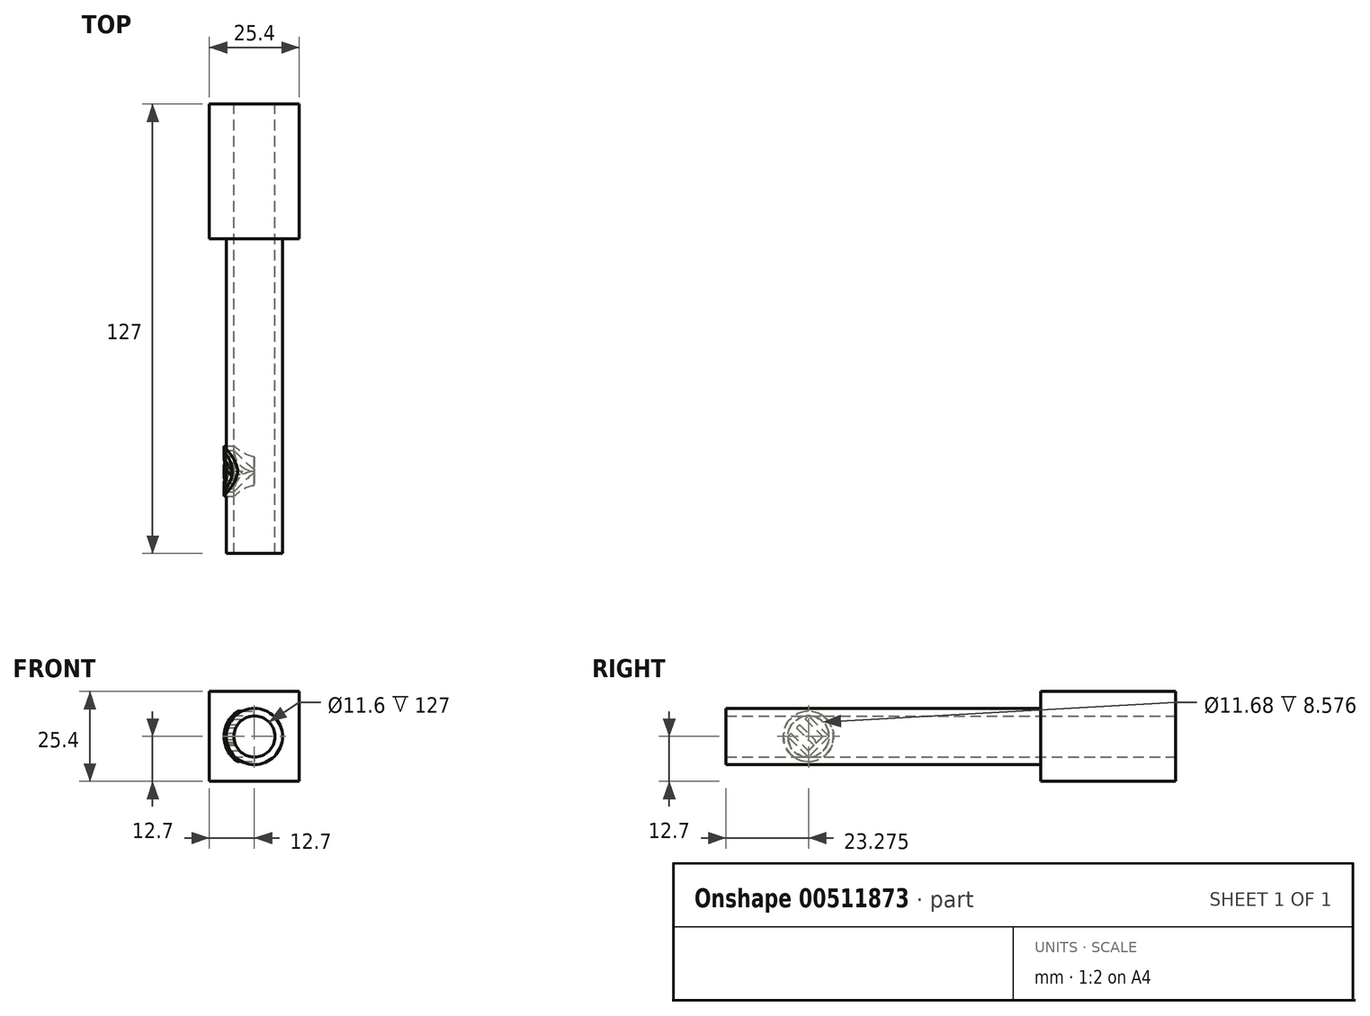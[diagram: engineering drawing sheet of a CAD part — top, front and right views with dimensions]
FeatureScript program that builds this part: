
annotation { "Feature Type Name" : "Feature", "Feature Type Description" : "" }
export const myFeature = defineFeature(function(context is Context, id is Id, definition is map)
    precondition{}
    {
        {
            var Q0;
            Q0=qCreatedBy(makeId("Front.planeOp"),FACE);
            var sketch = newSketch(context, id + "F0", { "sketchPlane" : qUnion([Q0])});
            skLineSegment(sketch, "E0.bottom", {"start": v(12.7, -12.7) * mm, "end": v(-12.7, -12.7) * mm});
            skLineSegment(sketch, "E0.top", {"start": v(12.7, 12.7) * mm, "end": v(-12.7, 12.7) * mm});
            skLineSegment(sketch, "E0.left", {"start": v(12.7, -12.7) * mm, "end": v(12.7, 12.7) * mm});
            skLineSegment(sketch, "E0.right", {"start": v(-12.7, -12.7) * mm, "end": v(-12.7, 12.7) * mm});
            skPoint(sketch, "E0.middle", {"position": v(0, 0) * mm});
            skCircle(sketch, "E1", {"center": v(0, 0) * mm, "radius": 7.94 * mm});
            skCircle(sketch, "E2", {"center": v(0, 0) * mm, "radius": 5.8 * mm});
            skSolve(sketch);
        }
        {
            var Q0;
            Q0=qSketchRegion(id+"F0",true);
            var Q1;
            Q1=makeQuery(id+"F0.imprint","IMPRINT",FACE,{"disambiguationData":[TD([[makeQuery(id+"F0.imprint","IMPRINT",EDGE,{"derivedFrom":sQuery(id+"F0.wireOp",EDGE,"E1")}),1.0]])]});
            extrude(context, id + "F1", {"entities" : qUnion([Q0, Q1]), "depth" : 38.1 * mm});
        }
        {
            var Q0;
            Q0=makeQuery(id+"F0.imprint","IMPRINT",FACE,{"disambiguationData":[TD([[makeQuery(id+"F0.imprint","IMPRINT",EDGE,{"derivedFrom":sQuery(id+"F0.wireOp",EDGE,"E1")}),1.0]])]});
            extrude(context, id + "F2", {"entities" : qUnion([Q0]), "operationType" : NewBodyOperationType.ADD, "depth" : 127 * mm, "offsetDistance" : 25.4 * mm});
        }
        {
            var Q0;
            Q0=qCreatedBy(makeId("Right.planeOp"),FACE);
            var sketch = newSketch(context, id + "F3", { "sketchPlane" : qUnion([Q0])});
            skCircle(sketch, "E3", {"center": v(-103.72, 0) * mm, "radius": 7.11 * mm});
            skCircle(sketch, "E4", {"center": v(-103.72, 0) * mm, "radius": 5.84 * mm});
            skLineSegment(sketch, "E5", {"start": v(-97.88, 0) * mm, "end": v(-103.72, 5.84) * mm});
            skLineSegment(sketch, "E6", {"start": v(-103.72, 5.84) * mm, "end": v(-104.62, 4.94) * mm});
            skLineSegment(sketch, "E7", {"start": v(-97.88, 0) * mm, "end": v(-103.72, -5.84) * mm});
            skLineSegment(sketch, "E8", {"start": v(-103.72, -5.84) * mm, "end": v(-109.57, 0) * mm});
            skLineSegment(sketch, "E9", {"start": v(-109.57, 0) * mm, "end": v(-108.67, 0.9) * mm});
            skLineSegment(sketch, "E10", {"start": v(-104.62, 4.94) * mm, "end": v(-99.68, 0) * mm});
            skLineSegment(sketch, "E11", {"start": v(-99.68, 0) * mm, "end": v(-101.28, -1.6) * mm});
            skLineSegment(sketch, "E12", {"start": v(-106.21, 3.34) * mm, "end": v(-107.1, 2.44) * mm});
            skLineSegment(sketch, "E13", {"start": v(-107.1, 2.44) * mm, "end": v(-102.17, -2.5) * mm});
            skLineSegment(sketch, "E14", {"start": v(-108.67, 0.9) * mm, "end": v(-103.73, -4.04) * mm});
            skLineSegment(sketch, "E15", {"start": v(-103.73, -4.04) * mm, "end": v(-102.17, -2.5) * mm});
            skLineSegment(sketch, "E16", {"start": v(-102, -0.87) * mm, "end": v(-101.63, -1.96) * mm});
            skLineSegment(sketch, "E17", {"start": v(-101.63, -1.96) * mm, "end": v(-101.28, -1.6) * mm});
            skLineSegment(sketch, "E18", {"start": v(-106.21, 3.34) * mm, "end": v(-102, -0.87) * mm});
            skSolve(sketch);
        }
        {
            var Q0;
            Q0=makeQuery(id+"F3.imprint","IMPRINT",FACE,{"disambiguationData":[TD([[makeQuery(id+"F3.imprint","IMPRINT",EDGE,{"derivedFrom":sQuery(id+"F3.wireOp",EDGE,"E3")}),1.0]])]});
            var Q1;
            Q1=makeQuery(id+"F3.imprint","IMPRINT",FACE,{"disambiguationData":[TD([[makeQuery(id+"F3.imprint","IMPRINT",EDGE,{"derivedFrom":sQuery(id+"F3.wireOp",EDGE,"E5")}),1.0]])]});
            extrude(context, id + "F4", {"entities" : qUnion([Q0, Q1]), "oppositeDirection" : true, "depth" : 12.7 * mm, "offsetDistance" : 25.4 * mm});
        }
        {
            var Q0;
            Q0=makeQuery(id+"F2.opExtrude","CAP_FACE",FACE,{"disambiguationData":[OSD([sQuery(id+"F0.wireOp",EDGE,"E1"),sQuery(id+"F0.wireOp",EDGE,"E2")])],"isStart":false});
            var sketch = newSketch(context, id + "F6", { "sketchPlane" : qUnion([Q0])});
            skCircle(sketch, "E19", {"center": v(0, 0) * mm, "radius": 4.74 * mm});
            skCircle(sketch, "E20", {"center": v(0, 0) * mm, "radius": 8.57 * mm});
            skCircle(sketch, "E21", {"center": v(0, 0) * mm, "radius": 29.4 * mm});
            skSolve(sketch);
        }
        {
            var Q0;
            Q0=makeQuery(id+"F6.imprint","IMPRINT",FACE,{"disambiguationData":[TD([[makeQuery(id+"F6.imprint","IMPRINT",EDGE,{"derivedFrom":sQuery(id+"F6.wireOp",EDGE,"E20")}),-1.0]])]});
            extrude(context, id + "F7", {"entities" : qUnion([Q0]), "operationType" : NewBodyOperationType.REMOVE, "oppositeDirection" : true, "depth" : 32.77 * mm, "offsetDistance" : 25.4 * mm});
        }
        {
            var Q0;
            Q0=makeQuery(id+"F0.imprint","IMPRINT",FACE,{"disambiguationData":[TD([[makeQuery(id+"F0.imprint","IMPRINT",EDGE,{"derivedFrom":sQuery(id+"F0.wireOp",EDGE,"E2")}),1.0]])]});
            extrude(context, id + "F8", {"entities" : qUnion([Q0]), "operationType" : NewBodyOperationType.REMOVE, "depth" : 152.4 * mm, "offsetDistance" : 25.4 * mm});
        }
    });
